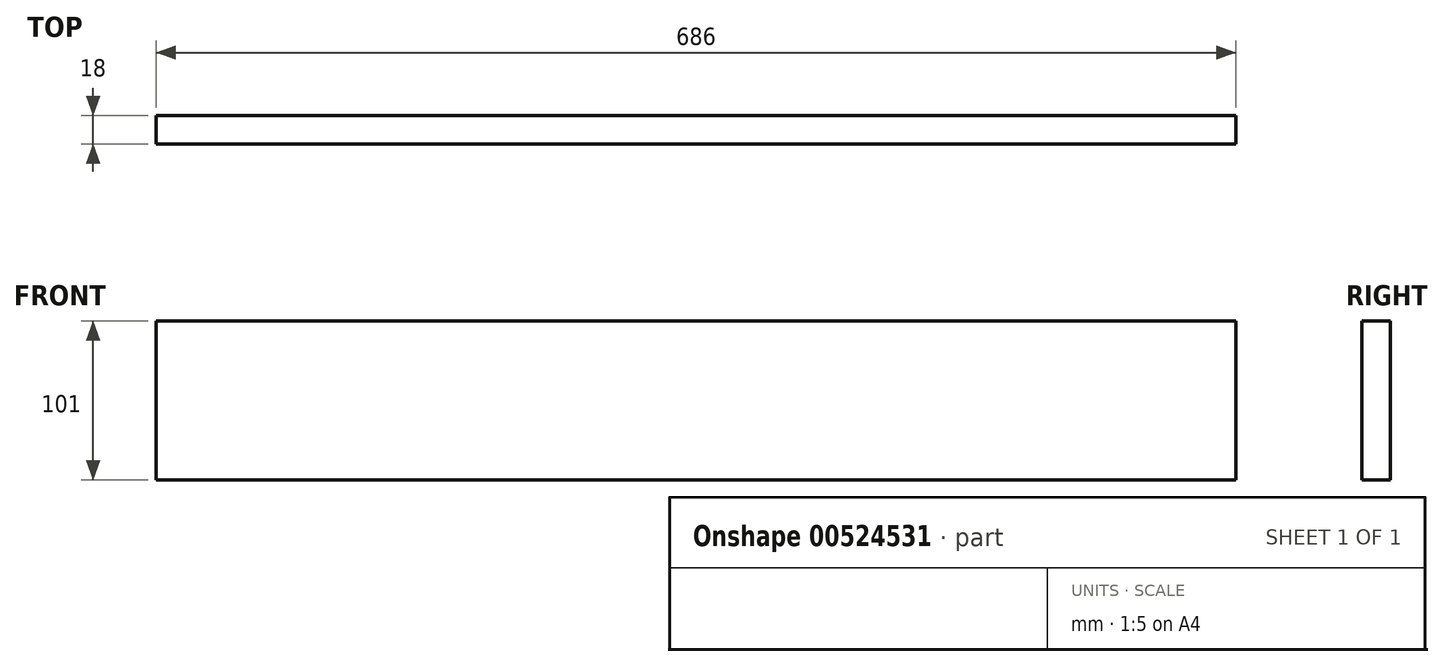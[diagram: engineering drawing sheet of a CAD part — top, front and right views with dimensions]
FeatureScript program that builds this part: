
annotation { "Feature Type Name" : "Feature", "Feature Type Description" : "" }
export const myFeature = defineFeature(function(context is Context, id is Id, definition is map)
    precondition{}
    {
        {
            var Q0;
            Q0=qCreatedBy(makeId("Front.planeOp"),FACE);
            var sketch = newSketch(context, id + "F0", { "sketchPlane" : qUnion([Q0])});
            skLineSegment(sketch, "E0.bottom", {"start": v(0, 0) * mm, "end": v(686, 0) * mm});
            skLineSegment(sketch, "E0.top", {"start": v(0, 101) * mm, "end": v(686, 101) * mm});
            skLineSegment(sketch, "E0.left", {"start": v(0, 0) * mm, "end": v(0, 101) * mm});
            skLineSegment(sketch, "E0.right", {"start": v(686, 0) * mm, "end": v(686, 101) * mm});
            skSolve(sketch);
        }
        {
            var Q0;
            Q0=qSketchRegion(id+"F0",true);
            extrude(context, id + "F1", {"entities" : qUnion([Q0]), "depth" : 18 * mm, "offsetDistance" : 25 * mm});
        }
    });
